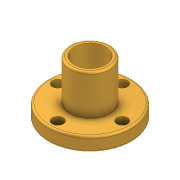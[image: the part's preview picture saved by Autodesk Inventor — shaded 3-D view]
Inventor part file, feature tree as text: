
AUTODESK INVENTOR PART (.ipt)
format: ipt  version: 2020 (Build 240168000, 168)  size: 145,920 bytes
history: native  units: mm
features: fillet x1
ambient origin geometry x8: Origin, YZ Plane, XZ Plane, XY Plane, X Axis, Y Axis, Z Axis, Center Point
bodies: Solid1 (feature_tree)
feature tree (1):
  fillet  "Fillet1"  [1 undecoded]
note: 1 required parameter value undecoded (feature->parameter linkage not recoverable at this tier; creation-order binding heuristic only, values carry confidence <= 0.55)
